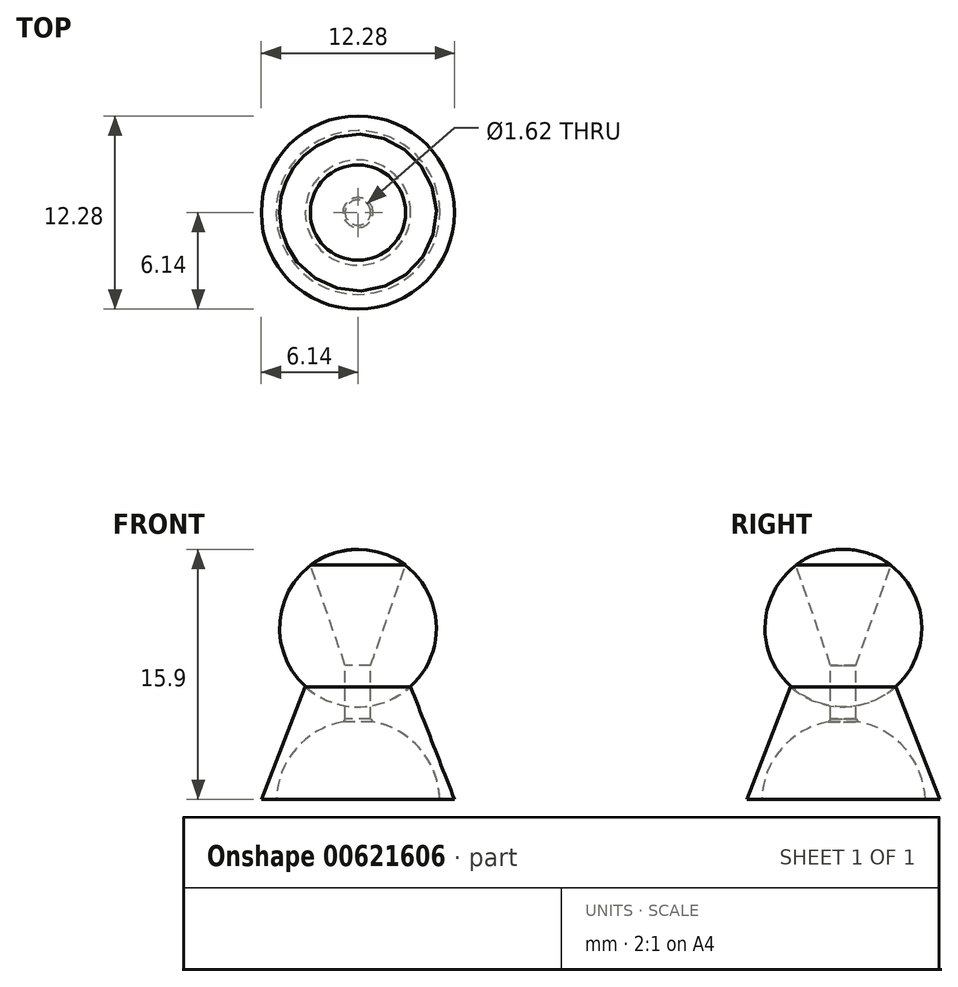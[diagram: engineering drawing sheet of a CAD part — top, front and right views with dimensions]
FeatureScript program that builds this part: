
annotation { "Feature Type Name" : "Feature", "Feature Type Description" : "" }
export const myFeature = defineFeature(function(context is Context, id is Id, definition is map)
    precondition{}
    {
        {
            var Q0;
            Q0=qCreatedBy(makeId("Front.planeOp"),FACE);
            var sketch = newSketch(context, id + "F0", { "sketchPlane" : qUnion([Q0])});
            skPoint(sketch, "E0.first.point", {"position": v(0, -4.33) * mm});
            skPoint(sketch, "E0.second.point", {"position": v(0, -2.56) * mm});
            skArc(sketch, "E1", {"start": v(-3.03, 12.5) * mm, "mid": v(-5.01, 8.7) * mm, "end": v(-3.35, 4.77) * mm});
            skPoint(sketch, "E1.first.point", {"position": v(0, 13.5) * mm});
            skPoint(sketch, "E1.second.point", {"position": v(0, 3.5) * mm});
            skPoint(sketch, "E1.third.point", {"position": v(-5, 8.94) * mm});
            skLineSegment(sketch, "E2", {"start": v(0, 13.5) * mm, "end": v(0, -4.33) * mm});
            skPoint(sketch, "E3.MirrorCS.end.orphan", {"position": v(6.35, -8.94) * mm});
            skPoint(sketch, "E3.MirrorCS.start.orphan", {"position": v(3.5, 4.9) * mm});
            skPoint(sketch, "E4.MirrorCS.end.orphan", {"position": v(5.1, -9.15) * mm});
            skLineSegment(sketch, "E5", {"start": v(-0.81, 6.14) * mm, "end": v(-3.03, 12.5) * mm});
            skArc(sketch, "E6", {"start": v(-0.95, 2.55) * mm, "mid": v(-3.95, 0.82) * mm, "end": v(-5.2, -2.4) * mm});
            skLineSegment(sketch, "E7", {"start": v(-0.81, 6.14) * mm, "end": v(-0.81, 2.73) * mm});
            skLineSegment(sketch, "E8", {"start": v(-5.2, -2.4) * mm, "end": v(-6.14, -2.4) * mm});
            skLineSegment(sketch, "E9", {"start": v(-6.14, -2.4) * mm, "end": v(-3.35, 4.77) * mm});
            skLineSegment(sketch, "E10", {"start": v(-0.81, 2.73) * mm, "end": v(-0.95, 2.55) * mm});
            skSolve(sketch);
        }
        {
            var Q0;
            Q0 = qSketchRegion(id + "F0", true);
            var Q1;
            Q1=sQuery(id+"F0.wireOp",EDGE,"E2");
            revolve(context, id + "F1", {"entities" : qUnion([Q0]), "axis" : qUnion([Q1]), "revolveType" : RevolveType.FULL});
        }
    });
